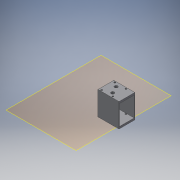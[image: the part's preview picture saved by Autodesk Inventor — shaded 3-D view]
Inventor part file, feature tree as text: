
AUTODESK INVENTOR PART (.ipt)
format: ipt  version: 2017 (Build 210142000, 142)  size: 230,400 bytes
history: native  units: mm
features: extrude x5, sketch x5, projected_geometry x5, other x3, plane x1, reference x1
ambient origin geometry x8: Origin, YZ Plane, XZ Plane, XY Plane, X Axis, Y Axis, Z Axis, Center Point
bodies: Solid1 (feature_tree)
feature tree (20):
  plane  "Work Plane1"
  extrude  "Extrusion1"  Depth=38.0mm
  extrude  "Extrusion2"  Depth=50.0mm TaperAngle=0.0deg
  extrude  "Extrusion3"  Depth=5.0mm TaperAngle=0.0deg
  extrude  "Extrusion4"  Depth=6.0mm
  extrude  "Extrusion5"  Depth=5.0mm TaperAngle=0.0deg
  sketch  "Sketch1"  dims[d0=3.81mm d1=38.0mm]
  reference  "Reference1"
  sketch  "Sketch2"  dims[d2=5.0mm d3=0.0mm d4=50.0mm d5=0.0mm]
  projected_geometry  "Projected Loop1"
  sketch  "Sketch3"  dims[d6=5.0mm d7=0.0mm d8=15.0mm d9=0.0mm]
  projected_geometry  "Projected Loop2"
  projected_geometry  "Projected Loop3"
  sketch  "Sketch4"  dims[d10=5.0mm d11=6.0mm]
  projected_geometry  "Projected Loop4"
  sketch  "Sketch5"  dims[d12=5.0mm d13=15.0mm d14=0.0mm]
  projected_geometry  "Projected Loop5"
  parser-record x1  (decoder bookkeeping rows leaked as tree rows — omitted from the tree; the rows remain in map.json)
  other  "gearbox.iam"
  other  "case part 1:1"
note: 1 file-system path scrubbed to <path> (originals preserved in map.json)
